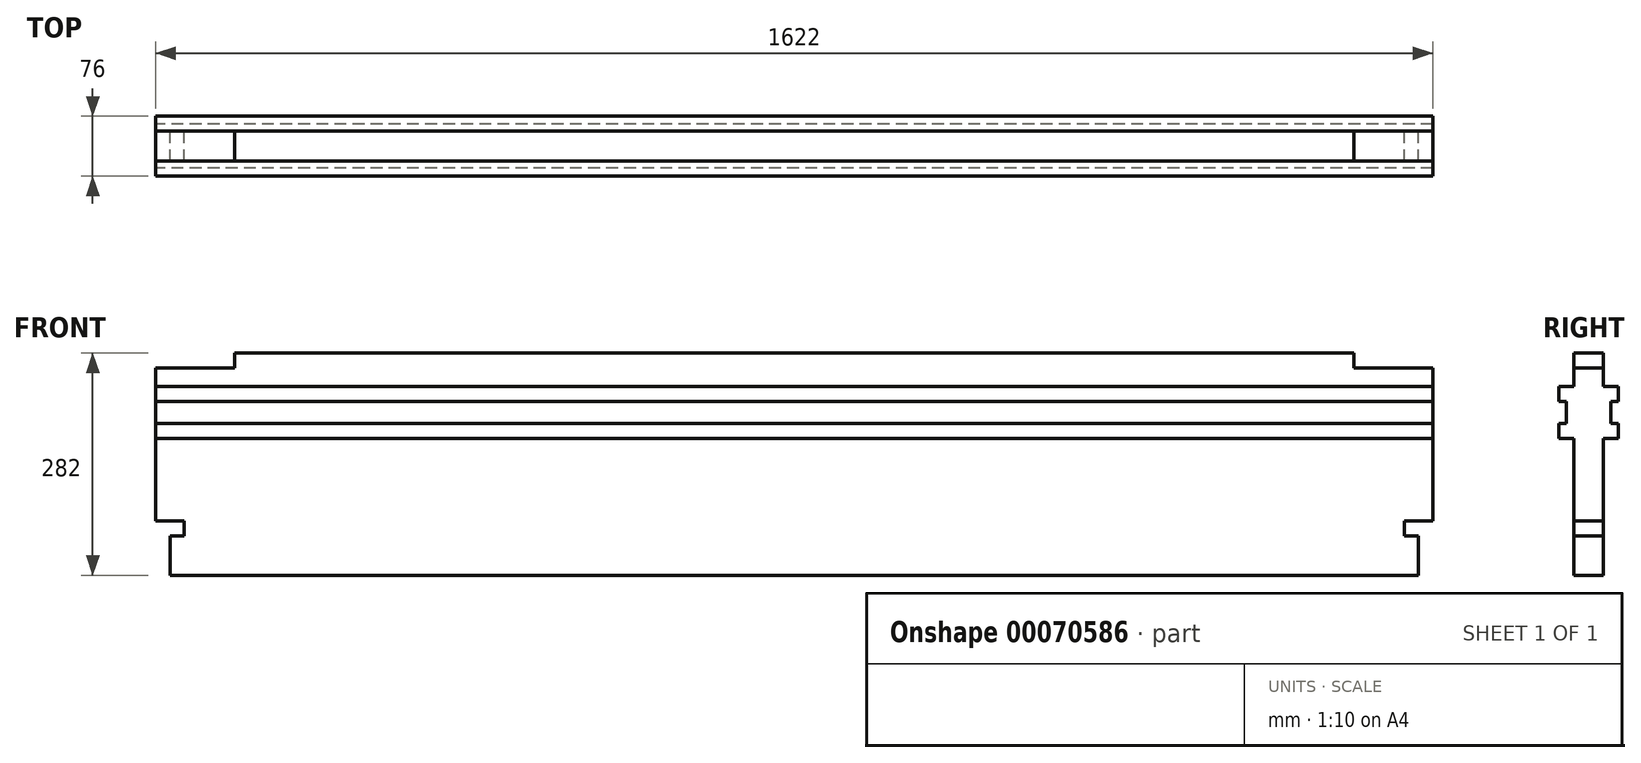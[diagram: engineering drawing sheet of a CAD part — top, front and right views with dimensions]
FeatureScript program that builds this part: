
annotation { "Feature Type Name" : "Feature", "Feature Type Description" : "" }
export const myFeature = defineFeature(function(context is Context, id is Id, definition is map)
    precondition{}
    {
        {
            var Q0;
            Q0=qCreatedBy(makeId("Front.planeOp"),FACE);
            var sketch = newSketch(context, id + "F0", { "sketchPlane" : qUnion([Q0])});
            skLineSegment(sketch, "E0", {"start": v(0, 0) * mm, "end": v(711, 0) * mm});
            skLineSegment(sketch, "E1", {"start": v(711, 0) * mm, "end": v(711, -19) * mm});
            skLineSegment(sketch, "E2", {"start": v(711, -19) * mm, "end": v(811, -19) * mm});
            skLineSegment(sketch, "E3", {"start": v(811, -19) * mm, "end": v(811, -213) * mm});
            skLineSegment(sketch, "E4", {"start": v(811, -213) * mm, "end": v(775, -213) * mm});
            skLineSegment(sketch, "E5", {"start": v(775, -213) * mm, "end": v(775, -232) * mm});
            skLineSegment(sketch, "E6", {"start": v(775, -232) * mm, "end": v(793, -232) * mm});
            skLineSegment(sketch, "E7", {"start": v(793, -232) * mm, "end": v(793, -282) * mm});
            skLineSegment(sketch, "E8", {"start": v(793, -282) * mm, "end": v(0, -282) * mm});
            skLineSegment(sketch, "E9", {"start": v(0, -282) * mm, "end": v(0, 0) * mm, "construction": true});
            skLineSegment(sketch, "E10.MirrorCS", {"start": v(-775, -232) * mm, "end": v(-793, -232) * mm});
            skLineSegment(sketch, "E11.MirrorCS", {"start": v(-775, -213) * mm, "end": v(-775, -232) * mm});
            skLineSegment(sketch, "E12.MirrorCS", {"start": v(-811, -213) * mm, "end": v(-775, -213) * mm});
            skLineSegment(sketch, "E13.MirrorCS", {"start": v(-711, 0) * mm, "end": v(-711, -19) * mm});
            skLineSegment(sketch, "E14.MirrorCS", {"start": v(-793, -232) * mm, "end": v(-793, -282) * mm});
            skLineSegment(sketch, "E15.MirrorCS", {"start": v(-711, -19) * mm, "end": v(-811, -19) * mm});
            skLineSegment(sketch, "E16.MirrorCS", {"start": v(-811, -19) * mm, "end": v(-811, -213) * mm});
            skLineSegment(sketch, "E17", {"start": v(-711, 0) * mm, "end": v(0, 0) * mm});
            skLineSegment(sketch, "E18", {"start": v(-793, -282) * mm, "end": v(0, -282) * mm});
            skSolve(sketch);
        }
        {
            var Q0;
            Q0 = qSketchRegion(id + "F0", true);
            extrude(context, id + "F1", {"entities" : qUnion([Q0]), "endBound" : BoundingType.SYMMETRIC, "depth" : 38 * mm});
        }
        {
            var Q0;
            Q0=qCreatedBy(makeId("Right.planeOp"),FACE);
            var sketch = newSketch(context, id + "F2", { "sketchPlane" : qUnion([Q0])});
            skLineSegment(sketch, "E19", {"start": v(-38, -42) * mm, "end": v(38, -42) * mm});
            skLineSegment(sketch, "E20", {"start": v(38, -42) * mm, "end": v(38, -61) * mm});
            skLineSegment(sketch, "E21", {"start": v(38, -61) * mm, "end": v(28, -61) * mm});
            skLineSegment(sketch, "E22", {"start": v(28, -61) * mm, "end": v(28, -89) * mm});
            skLineSegment(sketch, "E23", {"start": v(28, -89) * mm, "end": v(38, -89) * mm});
            skLineSegment(sketch, "E24", {"start": v(38, -89) * mm, "end": v(38, -108) * mm});
            skLineSegment(sketch, "E25", {"start": v(38, -108) * mm, "end": v(-38, -108) * mm});
            skLineSegment(sketch, "E26", {"start": v(-38, -108) * mm, "end": v(-38, -89) * mm});
            skLineSegment(sketch, "E27", {"start": v(-38, -89) * mm, "end": v(-28, -89) * mm});
            skLineSegment(sketch, "E28", {"start": v(-28, -89) * mm, "end": v(-28, -61) * mm});
            skLineSegment(sketch, "E29", {"start": v(-28, -61) * mm, "end": v(-38, -61) * mm});
            skLineSegment(sketch, "E30", {"start": v(-38, -61) * mm, "end": v(-38, -42) * mm});
            skSolve(sketch);
        }
        {
            var Q0;
            Q0 = qSketchRegion(id + "F2", true);
            extrude(context, id + "F3", {"entities" : qUnion([Q0]), "operationType" : NewBodyOperationType.ADD, "endBound" : BoundingType.SYMMETRIC, "depth" : 1622 * mm});
        }
    });
